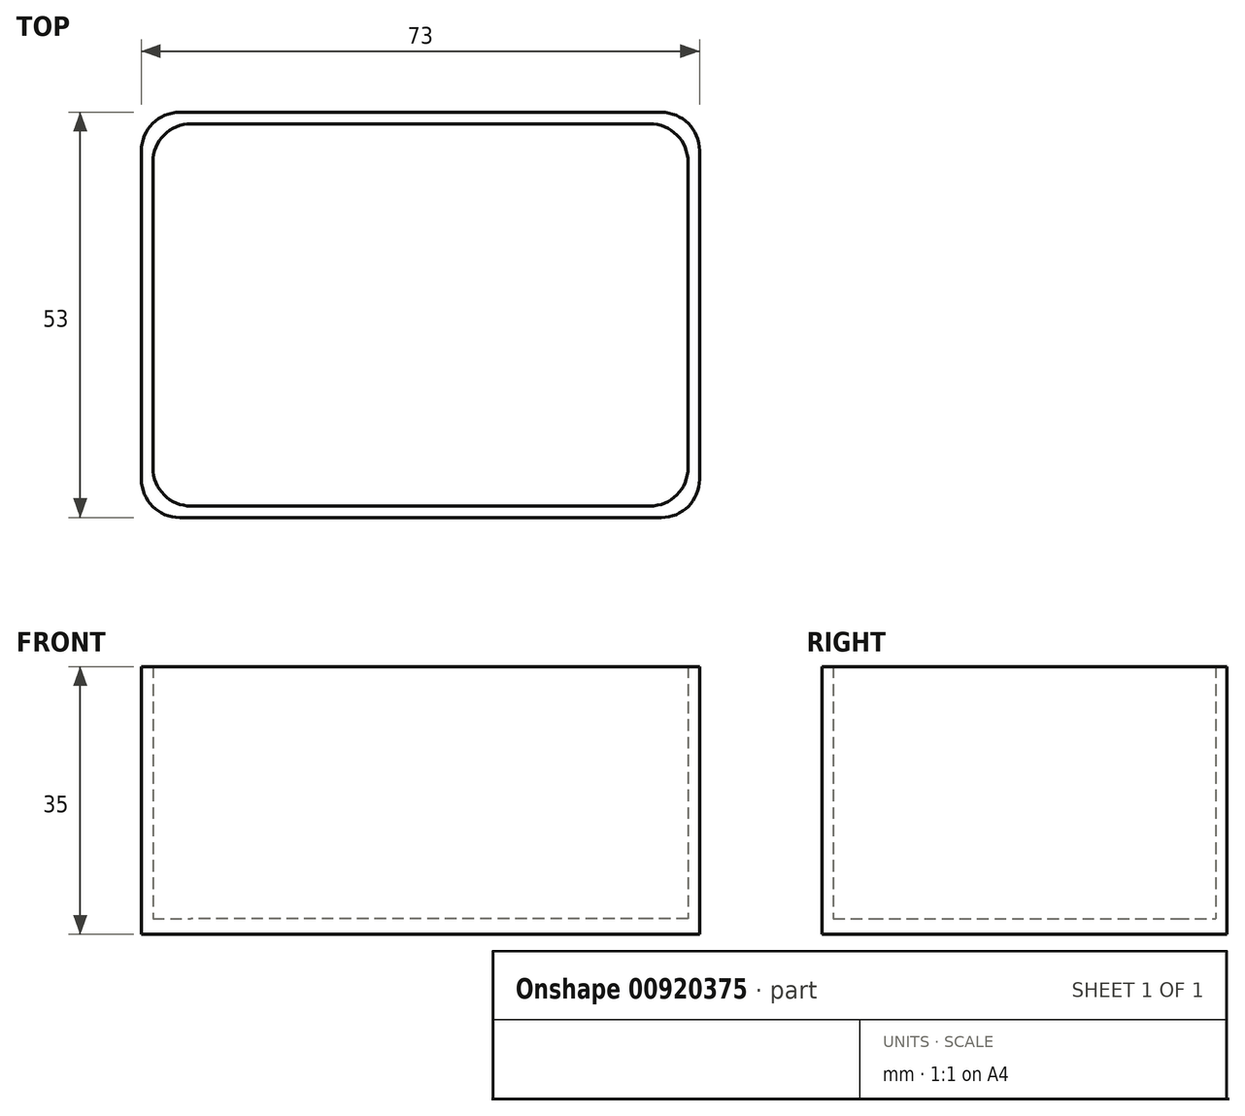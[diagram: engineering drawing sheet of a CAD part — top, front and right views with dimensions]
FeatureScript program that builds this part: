
annotation { "Feature Type Name" : "Feature", "Feature Type Description" : "" }
export const myFeature = defineFeature(function(context is Context, id is Id, definition is map)
    precondition{}
    {
        {
            var Q0;
            Q0=qCreatedBy(makeId("Top.planeOp"),FACE);
            var sketch = newSketch(context, id + "F0", { "sketchPlane" : qUnion([Q0])});
            skLineSegment(sketch, "E0.bottom", {"start": v(-30, 25) * mm, "end": v(30, 25) * mm});
            skLineSegment(sketch, "E0.top", {"start": v(-30, -25) * mm, "end": v(30, -25) * mm});
            skLineSegment(sketch, "E0.left", {"start": v(-35, 20) * mm, "end": v(-35, -20) * mm});
            skLineSegment(sketch, "E0.right", {"start": v(35, 20) * mm, "end": v(35, -20) * mm});
            skPoint(sketch, "E0.middle", {"position": v(0, 0) * mm});
            skLineSegment(sketch, "E1.bottom", {"start": v(-31.5, 26.5) * mm, "end": v(31.5, 26.5) * mm});
            skLineSegment(sketch, "E1.top", {"start": v(-31.5, -26.5) * mm, "end": v(31.5, -26.5) * mm});
            skLineSegment(sketch, "E1.left", {"start": v(-36.5, 21.5) * mm, "end": v(-36.5, -21.5) * mm});
            skLineSegment(sketch, "E1.right", {"start": v(36.5, 21.5) * mm, "end": v(36.5, -21.5) * mm});
            skPoint(sketch, "E2.visualSharp", {"position": v(-35, 25) * mm});
            skArc(sketch, "E2.filletArc", {"start": v(-30, 25) * mm, "mid": v(-33.54, 23.54) * mm, "end": v(-35, 20) * mm});
            skPoint(sketch, "E3.visualSharp", {"position": v(-36.5, 26.5) * mm});
            skArc(sketch, "E3.filletArc", {"start": v(-31.5, 26.5) * mm, "mid": v(-35.04, 25.04) * mm, "end": v(-36.5, 21.5) * mm});
            skPoint(sketch, "E4.visualSharp", {"position": v(36.5, 26.5) * mm});
            skArc(sketch, "E4.filletArc", {"start": v(36.5, 21.5) * mm, "mid": v(35.04, 25.04) * mm, "end": v(31.5, 26.5) * mm});
            skPoint(sketch, "E5.visualSharp", {"position": v(35, 25) * mm});
            skArc(sketch, "E5.filletArc", {"start": v(35, 20) * mm, "mid": v(33.54, 23.54) * mm, "end": v(30, 25) * mm});
            skPoint(sketch, "E6.visualSharp", {"position": v(35, -25) * mm});
            skArc(sketch, "E6.filletArc", {"start": v(30, -25) * mm, "mid": v(33.54, -23.54) * mm, "end": v(35, -20) * mm});
            skPoint(sketch, "E7.visualSharp", {"position": v(36.5, -26.5) * mm});
            skArc(sketch, "E7.filletArc", {"start": v(31.5, -26.5) * mm, "mid": v(35.04, -25.04) * mm, "end": v(36.5, -21.5) * mm});
            skPoint(sketch, "E8.visualSharp", {"position": v(-36.5, -26.5) * mm});
            skArc(sketch, "E8.filletArc", {"start": v(-36.5, -21.5) * mm, "mid": v(-35.04, -25.04) * mm, "end": v(-31.5, -26.5) * mm});
            skPoint(sketch, "E9.visualSharp", {"position": v(-35, -25) * mm});
            skArc(sketch, "E9.filletArc", {"start": v(-35, -20) * mm, "mid": v(-33.54, -23.54) * mm, "end": v(-30, -25) * mm});
            skSolve(sketch);
        }
        {
            var Q0;
            Q0=makeQuery(id+"F0.imprint","IMPRINT",FACE,{"disambiguationData":[TD([[makeQuery(id+"F0.imprint","IMPRINT",EDGE,{"derivedFrom":sQuery(id+"F0.wireOp",EDGE,"E0.bottom")}),-1.0]])]});
            var Q1;
            Q1=makeQuery(id+"F0.imprint","IMPRINT",FACE,{"disambiguationData":[TD([[makeQuery(id+"F0.imprint","IMPRINT",EDGE,{"derivedFrom":sQuery(id+"F0.wireOp",EDGE,"E0.bottom")}),1.0]])]});
            extrude(context, id + "F1", {"entities" : qUnion([Q0, Q1]), "depth" : 2 * mm, "offsetDistance" : 25 * mm});
        }
        {
            var Q0;
            Q0=makeQuery(id+"F0.imprint","IMPRINT",FACE,{"disambiguationData":[TD([[makeQuery(id+"F0.imprint","IMPRINT",EDGE,{"derivedFrom":sQuery(id+"F0.wireOp",EDGE,"E0.bottom")}),1.0]])]});
            extrude(context, id + "F2", {"entities" : qUnion([Q0]), "operationType" : NewBodyOperationType.ADD, "depth" : 35 * mm, "offsetDistance" : 25 * mm});
        }
    });
